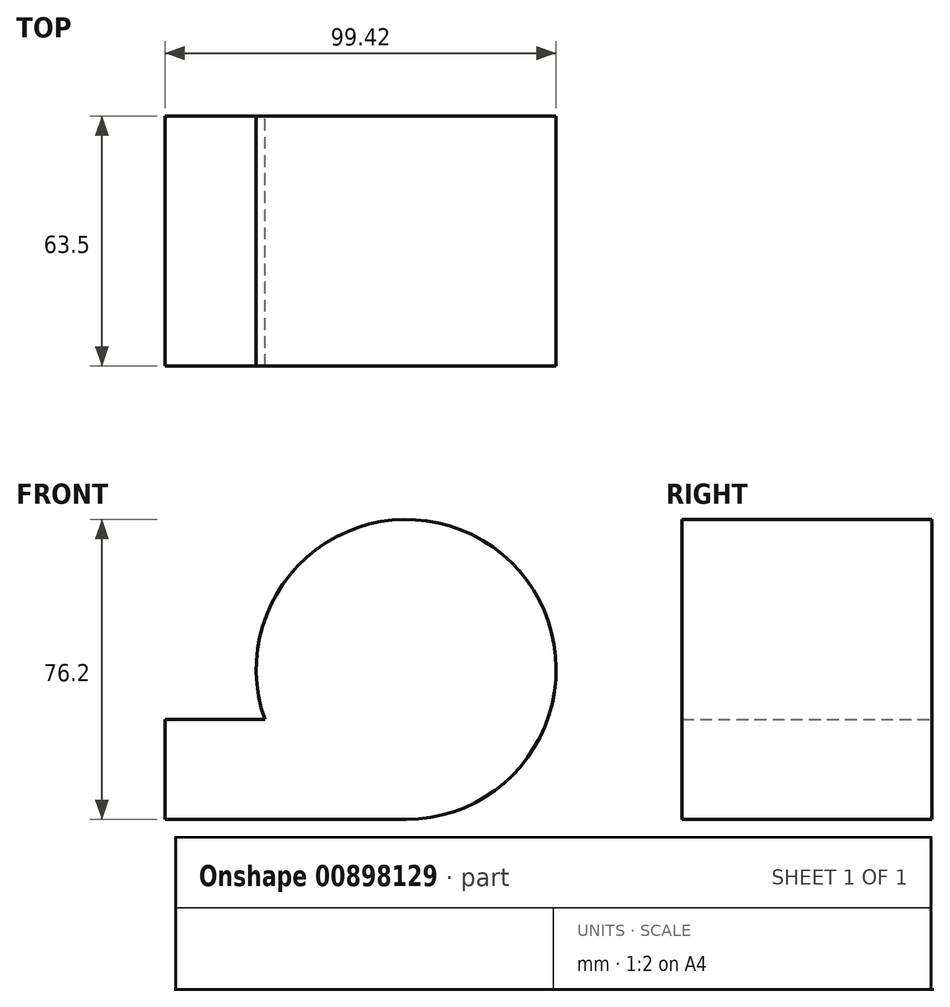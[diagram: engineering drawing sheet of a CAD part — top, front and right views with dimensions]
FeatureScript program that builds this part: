
annotation { "Feature Type Name" : "Feature", "Feature Type Description" : "" }
export const myFeature = defineFeature(function(context is Context, id is Id, definition is map)
    precondition{}
    {
        {
            var Q0;
            Q0=qCreatedBy(makeId("Front.planeOp"),FACE);
            var sketch = newSketch(context, id + "F0", { "sketchPlane" : qUnion([Q0])});
            skLineSegment(sketch, "E0", {"start": v(0, 0) * mm, "end": v(35.92, 0) * mm});
            skArc(sketch, "E1", {"start": v(35.92, 0) * mm, "mid": v(57.92, 69.2) * mm, "end": v(0, 25.4) * mm});
            skLineSegment(sketch, "E2", {"start": v(0, 25.4) * mm, "end": v(-25.4, 25.4) * mm});
            skLineSegment(sketch, "E3", {"start": v(-25.4, 25.4) * mm, "end": v(-25.4, 0) * mm});
            skLineSegment(sketch, "E4", {"start": v(-25.4, 0) * mm, "end": v(13.95, 0) * mm});
            skSolve(sketch);
        }
        {
            var Q0;
            Q0 = qSketchRegion(id + "F0", true);
            extrude(context, id + "F1", {"entities" : qUnion([Q0]), "depth" : 63.5 * mm, "offsetDistance" : 25.4 * mm});
        }
    });
